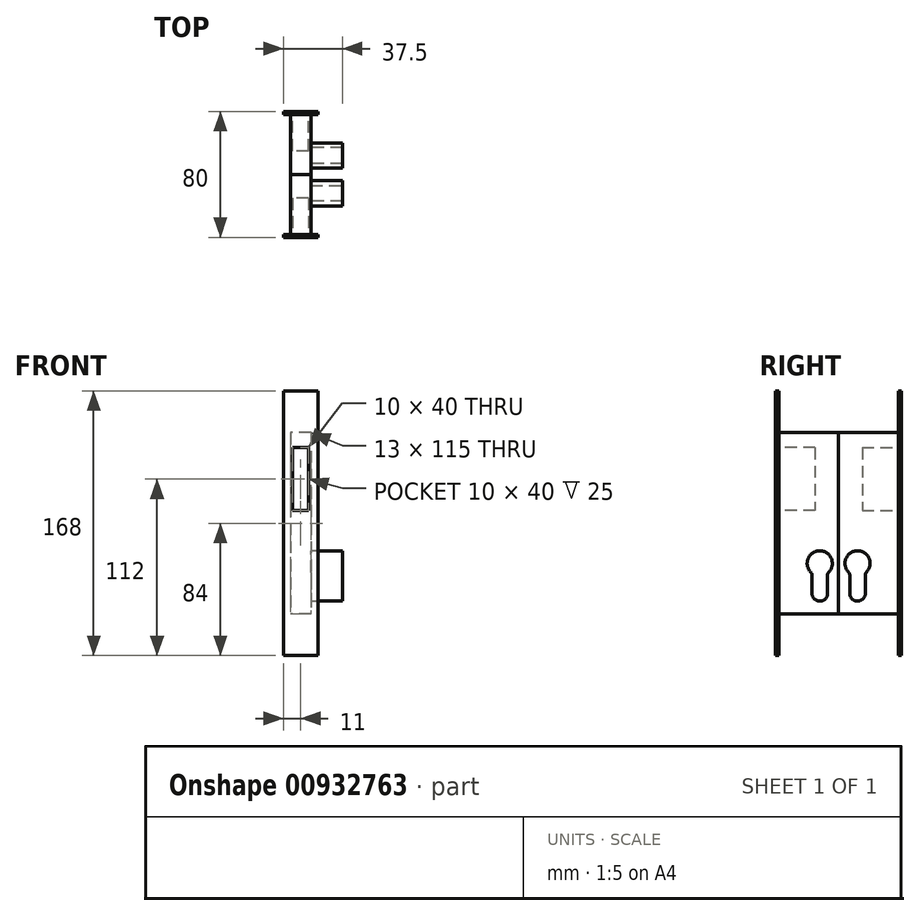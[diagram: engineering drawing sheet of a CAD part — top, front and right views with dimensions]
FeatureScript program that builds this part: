
annotation { "Feature Type Name" : "Feature", "Feature Type Description" : "" }
export const myFeature = defineFeature(function(context is Context, id is Id, definition is map)
    precondition{}
    {
        {
            var Q0;
            Q0=qCreatedBy(makeId("Top.planeOp"),FACE);
            var sketch = newSketch(context, id + "F0", { "sketchPlane" : qUnion([Q0])});
            skLineSegment(sketch, "E0.bottom", {"start": v(6.5, 19) * mm, "end": v(-6.5, 19) * mm});
            skLineSegment(sketch, "E0.top", {"start": v(6.5, -19) * mm, "end": v(-6.5, -19) * mm});
            skLineSegment(sketch, "E0.left", {"start": v(6.5, 19) * mm, "end": v(6.5, -19) * mm});
            skLineSegment(sketch, "E0.right", {"start": v(-6.5, 19) * mm, "end": v(-6.5, -19) * mm});
            skPoint(sketch, "E0.middle", {"position": v(0, 0) * mm});
            skSolve(sketch);
        }
        {
            var Q0;
            Q0 = qSketchRegion(id + "F0", true);
            extrude(context, id + "F1", {"entities" : qUnion([Q0]), "endBound" : BoundingType.SYMMETRIC, "depth" : 115 * mm, "offsetDistance" : 25 * mm});
        }
        {
            var Q0;
            Q0=qCreatedBy(makeId("Top.planeOp"),FACE);
            var sketch = newSketch(context, id + "F2", { "sketchPlane" : qUnion([Q0])});
            skLineSegment(sketch, "E1.bottom", {"start": v(-11, 19) * mm, "end": v(11, 19) * mm});
            skLineSegment(sketch, "E1.top", {"start": v(-11, 21) * mm, "end": v(11, 21) * mm});
            skLineSegment(sketch, "E1.left", {"start": v(-11, 19) * mm, "end": v(-11, 21) * mm});
            skLineSegment(sketch, "E1.right", {"start": v(11, 19) * mm, "end": v(11, 21) * mm});
            skSolve(sketch);
        }
        {
            var Q0;
            Q0=makeQuery(id+"F2.imprint","IMPRINT",FACE,{"disambiguationData":[TD([[makeQuery(id+"F2.imprint","IMPRINT",EDGE,{"derivedFrom":sQuery(id+"F2.wireOp",EDGE,"E1.bottom")}),1.0]])]});
            extrude(context, id + "F3", {"entities" : qUnion([Q0]), "operationType" : NewBodyOperationType.ADD, "endBound" : BoundingType.SYMMETRIC, "depth" : 168 * mm, "offsetDistance" : 25 * mm});
        }
        {
            var Q0;
            Q0=makeQuery(id+"F1.opExtrude","SWEPT_FACE",FACE,{"disambiguationData":[OSD([sQuery(id+"F0.wireOp",EDGE,"E0.left")])]});
            var sketch = newSketch(context, id + "F4", { "sketchPlane" : qUnion([Q0])});
            skLineSegment(sketch, "E2.top", {"start": v(-2, -49.5) * mm, "end": v(-12, -49.5) * mm});
            skLineSegment(sketch, "E2.left", {"start": v(-2, -31.74) * mm, "end": v(-2, -49.5) * mm});
            skLineSegment(sketch, "E2.right", {"start": v(-12, -31.74) * mm, "end": v(-12, -49.5) * mm});
            skArc(sketch, "E3", {"start": v(-2, -31.74) * mm, "mid": v(-7, -17.5) * mm, "end": v(-12, -31.74) * mm});
            skPoint(sketch, "E4.orphan", {"position": v(-12, -25.5) * mm});
            skPoint(sketch, "E5.orphan", {"position": v(-2, -25.5) * mm});
            skSolve(sketch);
        }
        {
            var Q0;
            Q0=makeQuery(id+"F4.imprint","IMPRINT",FACE,{"disambiguationData":[TD([[makeQuery(id+"F4.imprint","IMPRINT",EDGE,{"derivedFrom":sQuery(id+"F4.wireOp",EDGE,"E2.top")}),-1.0]])]});
            extrude(context, id + "F5", {"entities" : qUnion([Q0]), "operationType" : NewBodyOperationType.ADD, "depth" : 20 * mm, "offsetDistance" : 25 * mm});
        }
        {
            var Q0;
            Q0=makeQuery(id+"F5.opExtrude","SWEPT_EDGE",EDGE,{"disambiguationData":[OSD([sQuery(id+"F4.wireOp",EDGE,"E2.left"),sQuery(id+"F4.wireOp",EDGE,"E3")])]});
            var Q1;
            Q1=makeQuery(id+"F5.opExtrude","SWEPT_EDGE",EDGE,{"disambiguationData":[OSD([sQuery(id+"F4.wireOp",EDGE,"E2.right"),sQuery(id+"F4.wireOp",EDGE,"E3")])]});
            fillet(context, id + "F6", {"entities" : qUnion([Q0, Q1]), "radius" : 2 * mm, "tangentPropagation" : true, "allowEdgeOverflow" : false});
        }
        {
            var Q0;
            Q0=makeQuery(id+"F5.opExtrude","SWEPT_EDGE",EDGE,{"disambiguationData":[OSD([sQuery(id+"F4.wireOp",EDGE,"E2.top"),sQuery(id+"F4.wireOp",EDGE,"E2.right")])]});
            var Q1;
            Q1=makeQuery(id+"F5.opExtrude","SWEPT_EDGE",EDGE,{"disambiguationData":[OSD([sQuery(id+"F4.wireOp",EDGE,"E2.top"),sQuery(id+"F4.wireOp",EDGE,"E2.left")])]});
            fillet(context, id + "F7", {"entities" : qUnion([Q0, Q1]), "radius" : 5 * mm, "tangentPropagation" : true, "allowEdgeOverflow" : false});
        }
        {
            var Q0;
            Q0=makeQuery(id+"F3.opExtrude","SWEPT_FACE",FACE,{"disambiguationData":[OSD([sQuery(id+"F2.wireOp",EDGE,"E1.top")])]});
            var sketch = newSketch(context, id + "F8", { "sketchPlane" : qUnion([Q0])});
            skLineSegment(sketch, "E6.bottom", {"start": v(-5, 48) * mm, "end": v(5, 48) * mm});
            skLineSegment(sketch, "E6.top", {"start": v(-5, 8) * mm, "end": v(5, 8) * mm});
            skLineSegment(sketch, "E6.left", {"start": v(-5, 48) * mm, "end": v(-5, 8) * mm});
            skLineSegment(sketch, "E6.right", {"start": v(5, 48) * mm, "end": v(5, 8) * mm});
            skSolve(sketch);
        }
        {
            var Q0;
            Q0 = qSketchRegion(id + "F8", true);
            extrude(context, id + "F9", {"entities" : qUnion([Q0]), "operationType" : NewBodyOperationType.REMOVE, "oppositeDirection" : true, "depth" : 25 * mm, "offsetDistance" : 25 * mm});
        }
        {
            var Q0;
            Q0=makeQuery(id+"F1.opExtrude","SWEPT_BODY",BODY,{"disambiguationData":[OSD([sQuery(id+"F0.wireOp",EDGE,"E0.bottom"),sQuery(id+"F0.wireOp",EDGE,"E0.top"),sQuery(id+"F0.wireOp",EDGE,"E0.left"),sQuery(id+"F0.wireOp",EDGE,"E0.right")])]});
            var Q1;
            Q1=makeQuery(id+"F1.opExtrude","SWEPT_FACE",FACE,{"disambiguationData":[OSD([sQuery(id+"F0.wireOp",EDGE,"E0.top")])]});
            mirror(context, id + "F10", {"entities" : qUnion([Q0]), "mirrorPlane" : qUnion([Q1])});
        }
    });
